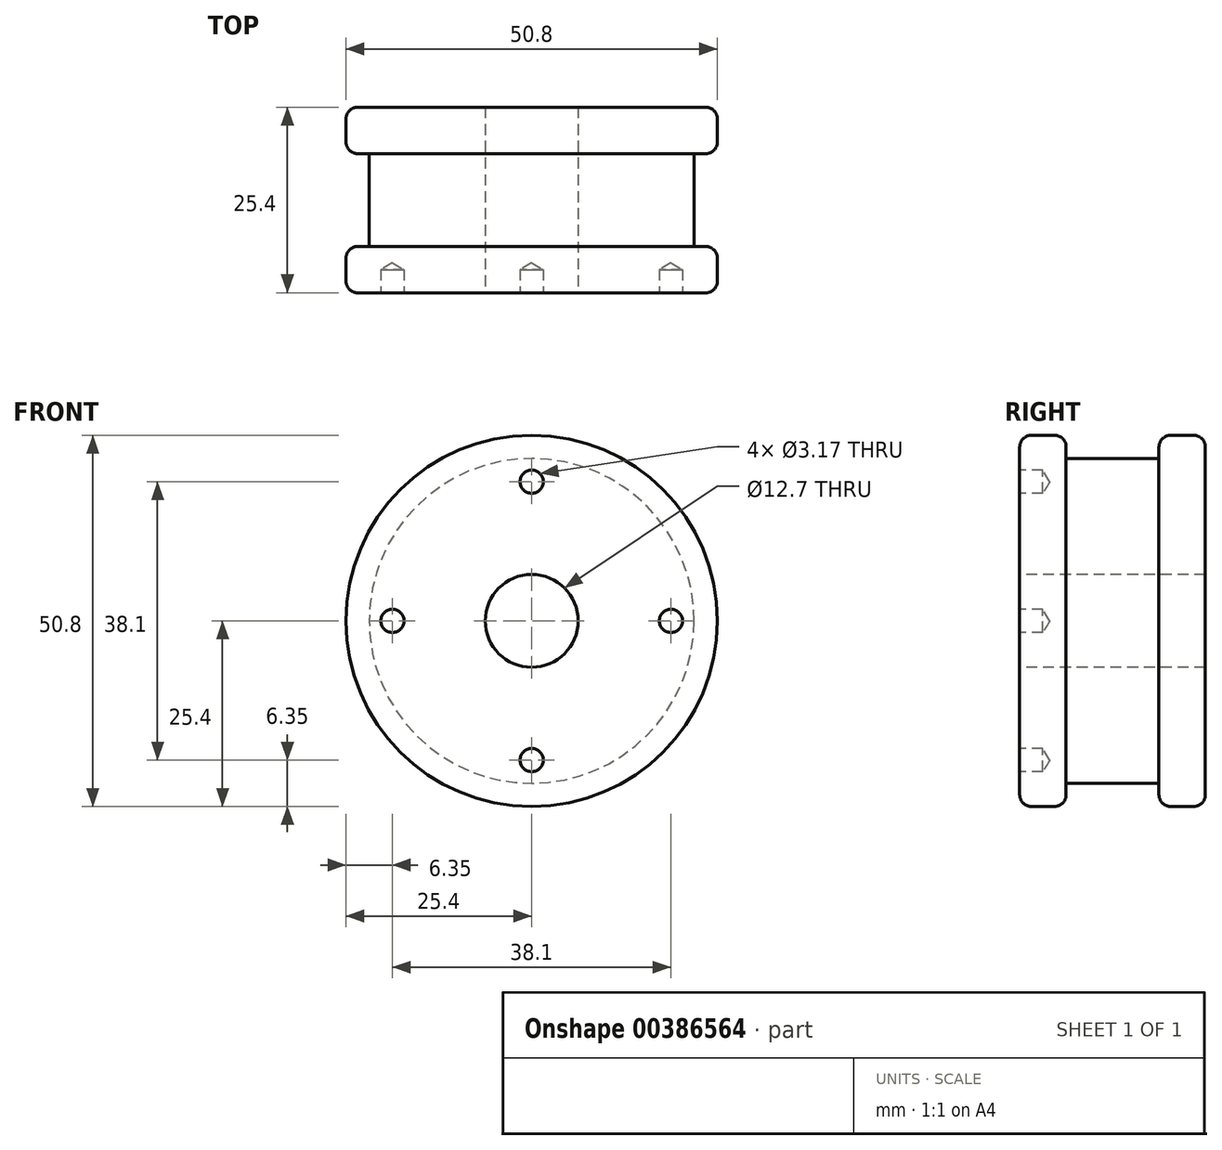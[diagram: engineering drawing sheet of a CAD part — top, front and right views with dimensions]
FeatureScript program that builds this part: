
annotation { "Feature Type Name" : "Feature", "Feature Type Description" : "" }
export const myFeature = defineFeature(function(context is Context, id is Id, definition is map)
    precondition{}
    {
        {
            var Q0;
            Q0=qCreatedBy(makeId("Front.planeOp"),FACE);
            var sketch = newSketch(context, id + "F0", { "sketchPlane" : qUnion([Q0])});
            skCircle(sketch, "E0", {"center": v(0, 0) * mm, "radius": 25.4 * mm});
            skSolve(sketch);
        }
        {
            var Q0;
            Q0 = qSketchRegion(id + "F0", true);
            extrude(context, id + "F1", {"entities" : qUnion([Q0]), "depth" : 6.35 * mm});
        }
        {
            var Q0;
            Q0=makeQuery(id+"F1.opExtrude","CAP_FACE",FACE,{"disambiguationData":[OSD([sQuery(id+"F0.wireOp",EDGE,"E0")])],"isStart":false});
            var sketch = newSketch(context, id + "F2", { "sketchPlane" : qUnion([Q0])});
            skCircle(sketch, "E1", {"center": v(0, 0) * mm, "radius": 22.23 * mm});
            skSolve(sketch);
        }
        {
            var Q0;
            Q0 = qSketchRegion(id + "F2", true);
            extrude(context, id + "F3", {"entities" : qUnion([Q0]), "operationType" : NewBodyOperationType.ADD, "depth" : 12.7 * mm});
        }
        {
            var Q0;
            Q0=makeQuery(id+"F3.opExtrude","CAP_FACE",FACE,{"disambiguationData":[OSD([sQuery(id+"F2.wireOp",EDGE,"E1")])],"isStart":false});
            var sketch = newSketch(context, id + "F4", { "sketchPlane" : qUnion([Q0])});
            skCircle(sketch, "E2", {"center": v(0, 0) * mm, "radius": 25.4 * mm});
            skSolve(sketch);
        }
        {
            var Q0;
            Q0 = qSketchRegion(id + "F4", true);
            extrude(context, id + "F5", {"entities" : qUnion([Q0]), "operationType" : NewBodyOperationType.ADD, "depth" : 6.35 * mm});
        }
        {
            var Q0;
            Q0=makeQuery(id+"F5.opExtrude","CAP_FACE",FACE,{"disambiguationData":[OSD([sQuery(id+"F4.wireOp",EDGE,"E2")])],"isStart":false});
            var sketch = newSketch(context, id + "F6", { "sketchPlane" : qUnion([Q0])});
            skPoint(sketch, "E3", {"position": v(0, 0) * mm});
            skPoint(sketch, "E4", {"position": v(0, 19.05) * mm});
            skPoint(sketch, "E5", {"position": v(19.05, 0) * mm});
            skPoint(sketch, "E6", {"position": v(0, -19.05) * mm});
            skPoint(sketch, "E7", {"position": v(-19.05, 0) * mm});
            skSolve(sketch);
        }
        {
            var Q0;
            Q0=sQuery(id+"F6.wireOp",VERTEX,"E4");
            var Q1;
            Q1=sQuery(id+"F6.wireOp",VERTEX,"E7");
            var Q2;
            Q2=sQuery(id+"F6.wireOp",VERTEX,"E6");
            var Q3;
            Q3=sQuery(id+"F6.wireOp",VERTEX,"E5");
            var Q4;
            Q4=makeQuery(id+"F1.opExtrude","SWEPT_BODY",BODY,{"disambiguationData":[OSD([sQuery(id+"F0.wireOp",EDGE,"E0")])]});
            hole(context, id + "F7", {"style" : HoleStyle.SIMPLE, "endStyle" : HoleEndStyle.BLIND, "holeDiameter" : 3.17 * mm, "holeDepth" : 3.17 * mm, "isTappedThrough" : true, "tappedDepth" : 12.7 * mm, "tapClearance" : 3, "locations" : qUnion([Q0, Q1, Q2, Q3]), "scope" : qUnion([Q4])});
        }
        {
            var Q0;
            Q0=sQuery(id+"F6.wireOp",VERTEX,"E3");
            var Q1;
            Q1=makeQuery(id+"F1.opExtrude","SWEPT_BODY",BODY,{"disambiguationData":[OSD([sQuery(id+"F0.wireOp",EDGE,"E0")])]});
            hole(context, id + "F8", {"style" : HoleStyle.SIMPLE, "endStyle" : HoleEndStyle.THROUGH, "holeDiameter" : 12.7 * mm, "isTappedThrough" : true, "tappedDepth" : 12.7 * mm, "tapClearance" : 3, "locations" : qUnion([Q0]), "scope" : qUnion([Q1])});
        }
        {
            var Q0;
            Q0=makeQuery(id+"F5.opExtrude","CAP_EDGE",EDGE,{"disambiguationData":[OSD([sQuery(id+"F4.wireOp",EDGE,"E2")])],"isStart":false});
            var Q1;
            Q1=makeQuery(id+"F1.opExtrude","CAP_EDGE",EDGE,{"disambiguationData":[OSD([sQuery(id+"F0.wireOp",EDGE,"E0")])],"isStart":false});
            var Q2;
            Q2=makeQuery(id+"F1.opExtrude","CAP_EDGE",EDGE,{"disambiguationData":[OSD([sQuery(id+"F0.wireOp",EDGE,"E0")])],"isStart":true});
            var Q3;
            Q3=makeQuery(id+"F5.opExtrude","CAP_EDGE",EDGE,{"disambiguationData":[OSD([sQuery(id+"F4.wireOp",EDGE,"E2")])],"isStart":true});
            var Q4;
            Q4=makeQuery(id+"F3.opExtrude","CAP_EDGE",EDGE,{"disambiguationData":[OSD([sQuery(id+"F2.wireOp",EDGE,"E1")])],"isStart":true});
            var Q5;
            Q5=makeQuery(id+"F3.opExtrude","CAP_EDGE",EDGE,{"disambiguationData":[OSD([sQuery(id+"F2.wireOp",EDGE,"E1")])],"isStart":false});
            fillet(context, id + "F9", {"entities" : qUnion([Q0, Q1, Q2, Q3, Q4, Q5]), "radius" : 1.59 * mm, "tangentPropagation" : true, "allowEdgeOverflow" : false});
        }
    });
